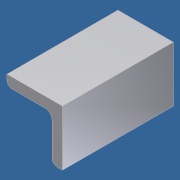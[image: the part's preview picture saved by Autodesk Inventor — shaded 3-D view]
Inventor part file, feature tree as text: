
AUTODESK INVENTOR PART (.ipt)
format: ipt  version: 2012 (Build 160160000, 160)  size: 79,360 bytes
history: native  units: in
note: dims shown in document units (in); Inventor stores cm internally (conversion verified against a paired STEP export)
features: extrude x1, sketch x1
ambient origin geometry x8: Origin, YZ Plane, XZ Plane, XY Plane, X Axis, Y Axis, Z Axis, Center Point
bodies: Solid1 (feature_tree)
feature tree (2):
  extrude  "Extrusion1"  Depth=0.1875in
  sketch  "Sketch1"  dims[d2=1.0in d3=0.1875in d4=0.125in d5=0.094in d6=2.0in d7=0.0in]
